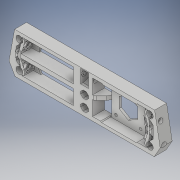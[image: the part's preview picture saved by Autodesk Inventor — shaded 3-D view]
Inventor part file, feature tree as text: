
AUTODESK INVENTOR PART (.ipt)
format: ipt  version: 2017 (Build 210142000, 142)  size: 568,832 bytes
history: native  units: in
note: dims shown in document units (in); Inventor stores cm internally (conversion verified against a paired STEP export)
features: fillet x1
ambient origin geometry x8: Origin, YZ Plane, XZ Plane, XY Plane, X Axis, Y Axis, Z Axis, Center Point
bodies: Solid1 (feature_tree)
feature tree (1):
  fillet  "Congé6"  [1 undecoded]
note: 1 required parameter value undecoded (feature->parameter linkage not recoverable at this tier; creation-order binding heuristic only, values carry confidence <= 0.55)
